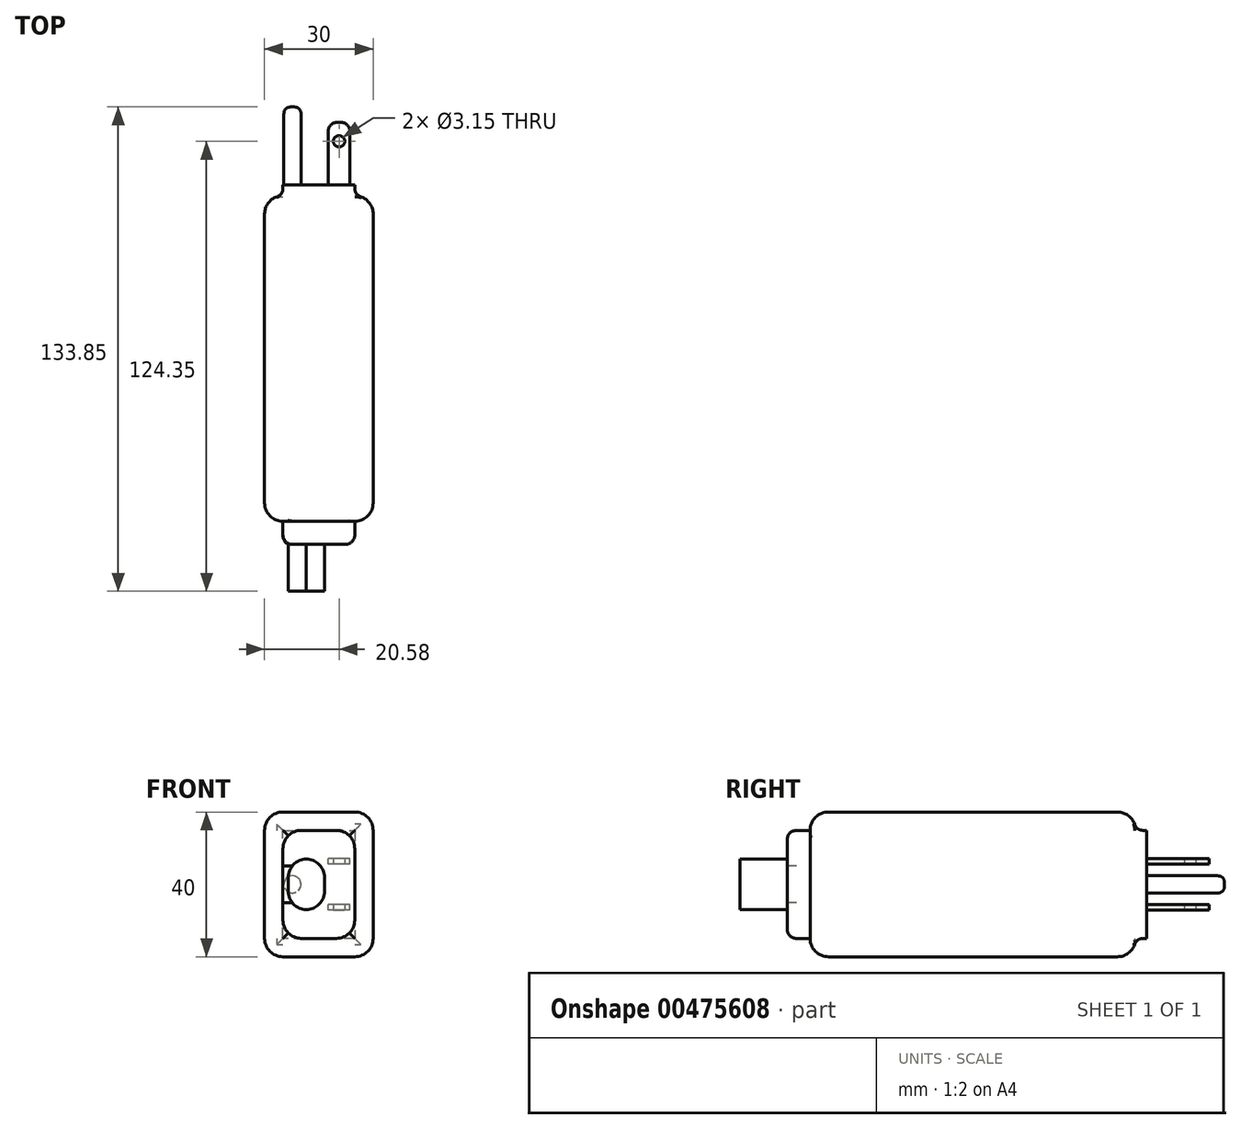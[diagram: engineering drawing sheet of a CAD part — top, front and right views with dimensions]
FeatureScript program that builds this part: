
annotation { "Feature Type Name" : "Feature", "Feature Type Description" : "" }
export const myFeature = defineFeature(function(context is Context, id is Id, definition is map)
    precondition{}
    {
        {
            var Q0;
            Q0=qCreatedBy(makeId("Top.planeOp"),FACE);
            var sketch = newSketch(context, id + "F0", { "sketchPlane" : qUnion([Q0])});
            skLineSegment(sketch, "E0.bottom", {"start": v(0, 0) * mm, "end": v(30, 0) * mm});
            skLineSegment(sketch, "E0.top", {"start": v(0, -90) * mm, "end": v(30, -90) * mm});
            skLineSegment(sketch, "E0.left", {"start": v(0, 0) * mm, "end": v(0, -90) * mm});
            skLineSegment(sketch, "E0.right", {"start": v(30, 0) * mm, "end": v(30, -90) * mm});
            skSolve(sketch);
        }
        {
            var Q0;
            Q0 = qSketchRegion(id + "F0", true);
            extrude(context, id + "F1", {"entities" : qUnion([Q0]), "depth" : 40 * mm});
        }
        {
            var Q0;
            Q0=makeQuery(id+"F1.opExtrude","CAP_EDGE",EDGE,{"disambiguationData":[OSD([sQuery(id+"F0.wireOp",EDGE,"E0.top")])],"isStart":false});
            var Q1;
            Q1=makeQuery(id+"F1.opExtrude","CAP_EDGE",EDGE,{"disambiguationData":[OSD([sQuery(id+"F0.wireOp",EDGE,"E0.bottom")])],"isStart":false});
            var Q2;
            Q2=makeQuery(id+"F1.opExtrude","CAP_EDGE",EDGE,{"disambiguationData":[OSD([sQuery(id+"F0.wireOp",EDGE,"E0.right")])],"isStart":false});
            var Q3;
            Q3=makeQuery(id+"F1.opExtrude","CAP_EDGE",EDGE,{"disambiguationData":[OSD([sQuery(id+"F0.wireOp",EDGE,"E0.left")])],"isStart":false});
            var Q4;
            Q4=makeQuery(id+"F1.opExtrude","CAP_EDGE",EDGE,{"disambiguationData":[OSD([sQuery(id+"F0.wireOp",EDGE,"E0.right")])],"isStart":true});
            var Q5;
            Q5=makeQuery(id+"F1.opExtrude","SWEPT_EDGE",EDGE,{"disambiguationData":[OSD([sQuery(id+"F0.wireOp",EDGE,"E0.top"),sQuery(id+"F0.wireOp",EDGE,"E0.right")])]});
            var Q6;
            Q6=makeQuery(id+"F1.opExtrude","SWEPT_EDGE",EDGE,{"disambiguationData":[OSD([sQuery(id+"F0.wireOp",EDGE,"E0.top"),sQuery(id+"F0.wireOp",EDGE,"E0.left")])]});
            var Q7;
            Q7=makeQuery(id+"F1.opExtrude","CAP_EDGE",EDGE,{"disambiguationData":[OSD([sQuery(id+"F0.wireOp",EDGE,"E0.top")])],"isStart":true});
            var Q8;
            Q8=makeQuery(id+"F1.opExtrude","SWEPT_EDGE",EDGE,{"disambiguationData":[OSD([sQuery(id+"F0.wireOp",EDGE,"E0.bottom"),sQuery(id+"F0.wireOp",EDGE,"E0.right")])]});
            var Q9;
            Q9=makeQuery(id+"F1.opExtrude","SWEPT_EDGE",EDGE,{"disambiguationData":[OSD([sQuery(id+"F0.wireOp",EDGE,"E0.bottom"),sQuery(id+"F0.wireOp",EDGE,"E0.left")])]});
            var Q10;
            Q10=makeQuery(id+"F1.opExtrude","CAP_EDGE",EDGE,{"disambiguationData":[OSD([sQuery(id+"F0.wireOp",EDGE,"E0.bottom")])],"isStart":true});
            var Q11;
            Q11=makeQuery(id+"F1.opExtrude","CAP_EDGE",EDGE,{"disambiguationData":[OSD([sQuery(id+"F0.wireOp",EDGE,"E0.left")])],"isStart":true});
            fillet(context, id + "F2", {"entities" : qUnion([Q0, Q1, Q2, Q3, Q4, Q5, Q6, Q7, Q8, Q9, Q10, Q11]), "radius" : 5.08 * mm, "tangentPropagation" : true, "allowEdgeOverflow" : false});
        }
        {
            var Q0;
            Q0=makeQuery(id+"F1.opExtrude","SWEPT_FACE",FACE,{"disambiguationData":[OSD([sQuery(id+"F0.wireOp",EDGE,"E0.bottom")])]});
            var sketch = newSketch(context, id + "F3", { "sketchPlane" : qUnion([Q0])});
            skLineSegment(sketch, "E1", {"start": v(-15, 34.92) * mm, "end": v(-15, 5.08) * mm, "construction": true});
            skLineSegment(sketch, "E2", {"start": v(-24.92, 20) * mm, "end": v(-5.08, 20) * mm, "construction": true});
            skLineSegment(sketch, "E3.bottom", {"start": v(-20, 23.5) * mm, "end": v(-10, 23.5) * mm});
            skLineSegment(sketch, "E3.top", {"start": v(-20, 16.5) * mm, "end": v(-10, 16.5) * mm});
            skLineSegment(sketch, "E3.left", {"start": v(-20, 23.5) * mm, "end": v(-20, 16.5) * mm});
            skLineSegment(sketch, "E3.right", {"start": v(-10, 23.5) * mm, "end": v(-10, 16.5) * mm});
            skSolve(sketch);
        }
        {
            var Q0;
            Q0=makeQuery(id+"F3.imprint","IMPRINT",FACE,{"disambiguationData":[TD([[makeQuery(id+"F3.imprint","IMPRINT",EDGE,{"derivedFrom":sQuery(id+"F3.wireOp",EDGE,"E3.bottom")}),1.0]])]});
            var Q1;
            Q1=makeQuery(id+"F3.imprint","IMPRINT",FACE,{"disambiguationData":[TD([[makeQuery(id+"F3.imprint","IMPRINT",EDGE,{"derivedFrom":sQuery(id+"F3.wireOp",EDGE,"E3.bottom")}),-1.0]])]});
            extrude(context, id + "F4", {"entities" : qUnion([Q0, Q1]), "operationType" : NewBodyOperationType.ADD, "depth" : 3 * mm});
        }
        {
            var Q0;
            {var subQ0=sQuery(id+"F0.wireOp",EDGE,"E0.left");var subQ1=sQuery(id+"F0.wireOp",EDGE,"E0.bottom");Q0=makeQuery(id+"F4.boolean.opBoolean","MERGE",EDGE,{"derivedFrom":[makeQuery(id+"F2.opFillet","BLEND_EDGE",EDGE,{"blendedFrom":[makeQuery(id+"F1.opExtrude","SWEPT_EDGE",EDGE,{"disambiguationData":[OSD([subQ1,subQ0])]}),makeQuery(id+"F1.opExtrude","SWEPT_FACE",FACE,{"disambiguationData":[OSD([subQ1])]})],"blendedInto":[makeQuery(id+"F1.opExtrude","SWEPT_FACE",FACE,{"disambiguationData":[OSD([subQ1])]})]}),makeQuery(id+"F4.opExtrude","CAP_EDGE",EDGE,{"disambiguationData":[OSD([subQ1,subQ0])],"isStart":true})]});}
            var Q1;
            {var subQ0=sQuery(id+"F0.wireOp",EDGE,"E0.bottom");var subQ1=makeQuery(id+"F2.opFillet","BLEND_EDGE",EDGE,{"blendedFrom":[makeQuery(id+"F1.opExtrude","CAP_EDGE",EDGE,{"disambiguationData":[OSD([subQ0])],"isStart":true}),makeQuery(id+"F1.opExtrude","SWEPT_FACE",FACE,{"disambiguationData":[OSD([subQ0])]})],"blendedInto":[makeQuery(id+"F1.opExtrude","SWEPT_FACE",FACE,{"disambiguationData":[OSD([subQ0])]})]});Q1=makeQuery(id+"F4.boolean.opBoolean","MERGE",EDGE,{"derivedFrom":[subQ1,makeQuery(id+"F4.opExtrude","CAP_EDGE",EDGE,{"disambiguationData":[OSD([subQ0]),TDD([makeQuery(id+"F3.imprint","IMPRINT",EDGE,{"derivedFrom":subQ1})])],"isStart":true})]});}
            var Q2;
            {var subQ0=sQuery(id+"F0.wireOp",EDGE,"E0.bottom");var subQ1=makeQuery(id+"F2.opFillet","BLEND_EDGE",EDGE,{"blendedFrom":[makeQuery(id+"F1.opExtrude","CAP_EDGE",EDGE,{"disambiguationData":[OSD([subQ0])],"isStart":false}),makeQuery(id+"F1.opExtrude","SWEPT_FACE",FACE,{"disambiguationData":[OSD([subQ0])]})],"blendedInto":[makeQuery(id+"F1.opExtrude","SWEPT_FACE",FACE,{"disambiguationData":[OSD([subQ0])]})]});Q2=makeQuery(id+"F4.boolean.opBoolean","MERGE",EDGE,{"derivedFrom":[subQ1,makeQuery(id+"F4.opExtrude","CAP_EDGE",EDGE,{"disambiguationData":[OSD([subQ0]),TDD([makeQuery(id+"F3.imprint","IMPRINT",EDGE,{"derivedFrom":subQ1})])],"isStart":true})]});}
            var Q3;
            {var subQ0=sQuery(id+"F0.wireOp",EDGE,"E0.right");var subQ1=sQuery(id+"F0.wireOp",EDGE,"E0.bottom");Q3=makeQuery(id+"F4.boolean.opBoolean","MERGE",EDGE,{"derivedFrom":[makeQuery(id+"F2.opFillet","BLEND_EDGE",EDGE,{"blendedFrom":[makeQuery(id+"F1.opExtrude","SWEPT_EDGE",EDGE,{"disambiguationData":[OSD([subQ1,subQ0])]}),makeQuery(id+"F1.opExtrude","SWEPT_FACE",FACE,{"disambiguationData":[OSD([subQ1])]})],"blendedInto":[makeQuery(id+"F1.opExtrude","SWEPT_FACE",FACE,{"disambiguationData":[OSD([subQ1])]})]}),makeQuery(id+"F4.opExtrude","CAP_EDGE",EDGE,{"disambiguationData":[OSD([subQ1,subQ0])],"isStart":true})]});}
            fillet(context, id + "F5", {"entities" : qUnion([Q0, Q1, Q2, Q3]), "radius" : 2.54 * mm, "tangentPropagation" : true, "rho" : 0.5, "crossSection" : FilletCrossSection.CONIC, "allowEdgeOverflow" : false});
        }
        {
            var Q0;
            Q0=makeQuery(id+"F4.opExtrude","CAP_FACE",FACE,{"disambiguationData":[OSD([sQuery(id+"F0.wireOp",EDGE,"E0.bottom"),sQuery(id+"F0.wireOp",EDGE,"E0.left"),sQuery(id+"F0.wireOp",EDGE,"E0.right")])],"isStart":false});
            var sketch = newSketch(context, id + "F6", { "sketchPlane" : qUnion([Q0])});
            skLineSegment(sketch, "E4", {"start": v(-24.92, 20) * mm, "end": v(-5.08, 20) * mm, "construction": true});
            skLineSegment(sketch, "E5", {"start": v(-15, 5.08) * mm, "end": v(-15, 34.92) * mm, "construction": true});
            skLineSegment(sketch, "E6.bottom", {"start": v(-23.58, 12.92) * mm, "end": v(-17.58, 12.92) * mm});
            skLineSegment(sketch, "E6.top", {"start": v(-23.58, 14.42) * mm, "end": v(-17.58, 14.42) * mm});
            skLineSegment(sketch, "E6.left", {"start": v(-23.58, 12.93) * mm, "end": v(-23.58, 14.42) * mm});
            skLineSegment(sketch, "E6.right", {"start": v(-17.58, 12.93) * mm, "end": v(-17.58, 14.43) * mm});
            skLineSegment(sketch, "E7.bottom", {"start": v(-23.58, 25.57) * mm, "end": v(-17.58, 25.57) * mm});
            skLineSegment(sketch, "E7.top", {"start": v(-23.58, 27.08) * mm, "end": v(-17.58, 27.08) * mm});
            skLineSegment(sketch, "E7.left", {"start": v(-23.58, 25.57) * mm, "end": v(-23.58, 27.08) * mm});
            skLineSegment(sketch, "E7.right", {"start": v(-17.58, 25.57) * mm, "end": v(-17.58, 27.08) * mm});
            skSolve(sketch);
        }
        {
            var Q0;
            Q0 = qSketchRegion(id + "F6", true);
            extrude(context, id + "F7", {"entities" : qUnion([Q0]), "operationType" : NewBodyOperationType.ADD, "depth" : 17.25 * mm});
        }
        {
            var Q0;
            Q0=makeQuery(id+"F7.opExtrude","CAP_EDGE",EDGE,{"disambiguationData":[OSD([sQuery(id+"F6.wireOp",EDGE,"E6.left")])],"isStart":false});
            var Q1;
            Q1=makeQuery(id+"F7.opExtrude","CAP_EDGE",EDGE,{"disambiguationData":[OSD([sQuery(id+"F6.wireOp",EDGE,"E7.left")])],"isStart":false});
            var Q2;
            Q2=makeQuery(id+"F7.opExtrude","CAP_EDGE",EDGE,{"disambiguationData":[OSD([sQuery(id+"F6.wireOp",EDGE,"E6.right")])],"isStart":false});
            var Q3;
            Q3=makeQuery(id+"F7.opExtrude","CAP_EDGE",EDGE,{"disambiguationData":[OSD([sQuery(id+"F6.wireOp",EDGE,"E7.right")])],"isStart":false});
            fillet(context, id + "F8", {"entities" : qUnion([Q0, Q1, Q2, Q3]), "radius" : 2.54 * mm, "tangentPropagation" : true, "allowEdgeOverflow" : false});
        }
        {
            var Q0;
            Q0=makeQuery(id+"F4.opExtrude","CAP_FACE",FACE,{"disambiguationData":[OSD([sQuery(id+"F0.wireOp",EDGE,"E0.bottom"),sQuery(id+"F0.wireOp",EDGE,"E0.left"),sQuery(id+"F0.wireOp",EDGE,"E0.right")])],"isStart":false});
            var sketch = newSketch(context, id + "F9", { "sketchPlane" : qUnion([Q0])});
            skCircle(sketch, "E8", {"center": v(-7.7, 20) * mm, "radius": 2.38 * mm});
            skLineSegment(sketch, "E9", {"start": v(-24.92, 20) * mm, "end": v(-5.08, 20) * mm, "construction": true});
            skSolve(sketch);
        }
        {
            var Q0;
            Q0 = qSketchRegion(id + "F9", true);
            extrude(context, id + "F10", {"entities" : qUnion([Q0]), "operationType" : NewBodyOperationType.ADD, "depth" : 21.5 * mm});
        }
        {
            var Q0;
            Q0=makeQuery(id+"F10.opExtrude","CAP_FACE",FACE,{"disambiguationData":[OSD([sQuery(id+"F9.wireOp",EDGE,"E8")])],"isStart":false});
            fillet(context, id + "F11", {"entities" : qUnion([Q0]), "radius" : 2 * mm, "tangentPropagation" : true, "rho" : 0.5, "crossSection" : FilletCrossSection.CONIC, "allowEdgeOverflow" : false});
        }
        {
            var Q0;
            Q0=makeQuery(id+"F7.opExtrude","SWEPT_FACE",FACE,{"disambiguationData":[OSD([sQuery(id+"F6.wireOp",EDGE,"E6.bottom")])]});
            var sketch = newSketch(context, id + "F12", { "sketchPlane" : qUnion([Q0])});
            skLineSegment(sketch, "E10", {"start": v(23.58, -15) * mm, "end": v(17.58, -15) * mm, "construction": true});
            skCircle(sketch, "E11", {"center": v(20.58, -15) * mm, "radius": 1.57 * mm});
            skSolve(sketch);
        }
        {
            var Q0;
            Q0 = qSketchRegion(id + "F12", true);
            extrude(context, id + "F13", {"entities" : qUnion([Q0]), "operationType" : NewBodyOperationType.REMOVE, "oppositeDirection" : true, "depth" : 25.4 * mm});
        }
        {
            var Q0;
            Q0=makeQuery(id+"F1.opExtrude","SWEPT_FACE",FACE,{"disambiguationData":[OSD([sQuery(id+"F0.wireOp",EDGE,"E0.top")])]});
            var sketch = newSketch(context, id + "F14", { "sketchPlane" : qUnion([Q0])});
            skLineSegment(sketch, "E12.0.0", {"start": v(5.08, 34.92) * mm, "end": v(5.08, 5.08) * mm});
            skLineSegment(sketch, "E12.0.1", {"start": v(5.08, 5.08) * mm, "end": v(24.92, 5.08) * mm});
            skLineSegment(sketch, "E12.0.2", {"start": v(24.92, 5.08) * mm, "end": v(24.92, 34.92) * mm});
            skLineSegment(sketch, "E12.0.3", {"start": v(24.92, 34.92) * mm, "end": v(5.08, 34.92) * mm});
            skSolve(sketch);
        }
        {
            var Q0;
            Q0 = qSketchRegion(id + "F14", true);
            extrude(context, id + "F15", {"entities" : qUnion([Q0]), "operationType" : NewBodyOperationType.ADD, "depth" : 6.35 * mm});
        }
        {
            var Q0;
            Q0=makeQuery(id+"F15.opExtrude","SWEPT_EDGE",EDGE,{"disambiguationData":[OSD([sQuery(id+"F14.wireOp",EDGE,"E12.0.1"),sQuery(id+"F14.wireOp",EDGE,"E12.0.2")])]});
            var Q1;
            Q1=makeQuery(id+"F15.opExtrude","SWEPT_EDGE",EDGE,{"disambiguationData":[OSD([sQuery(id+"F14.wireOp",EDGE,"E12.0.0"),sQuery(id+"F14.wireOp",EDGE,"E12.0.1")])]});
            var Q2;
            Q2=makeQuery(id+"F15.opExtrude","SWEPT_EDGE",EDGE,{"disambiguationData":[OSD([sQuery(id+"F14.wireOp",EDGE,"E12.0.2"),sQuery(id+"F14.wireOp",EDGE,"E12.0.3")])]});
            var Q3;
            Q3=makeQuery(id+"F15.opExtrude","SWEPT_EDGE",EDGE,{"disambiguationData":[OSD([sQuery(id+"F14.wireOp",EDGE,"E12.0.0"),sQuery(id+"F14.wireOp",EDGE,"E12.0.3")])]});
            fillet(context, id + "F16", {"entities" : qUnion([Q0, Q1, Q2, Q3]), "radius" : 5.08 * mm, "tangentPropagation" : true, "allowEdgeOverflow" : false});
        }
        {
            var Q0;
            Q0=makeQuery(id+"F15.opExtrude","CAP_FACE",FACE,{"disambiguationData":[OSD([sQuery(id+"F14.wireOp",EDGE,"E12.0.0"),sQuery(id+"F14.wireOp",EDGE,"E12.0.1"),sQuery(id+"F14.wireOp",EDGE,"E12.0.2"),sQuery(id+"F14.wireOp",EDGE,"E12.0.3")])],"isStart":false});
            var sketch = newSketch(context, id + "F17", { "sketchPlane" : qUnion([Q0])});
            skLineSegment(sketch, "E13.bottom", {"start": v(6.54, 27) * mm, "end": v(16.54, 27) * mm});
            skLineSegment(sketch, "E13.top", {"start": v(6.54, 13) * mm, "end": v(16.54, 13) * mm});
            skLineSegment(sketch, "E13.left", {"start": v(6.54, 27) * mm, "end": v(6.54, 13) * mm});
            skLineSegment(sketch, "E13.right", {"start": v(16.54, 27) * mm, "end": v(16.54, 13) * mm});
            skPoint(sketch, "E13.middle", {"position": v(11.54, 20) * mm});
            skPoint(sketch, "E13.middle.positionSnap0", {"position": v(5.08, 20) * mm});
            skPoint(sketch, "E13.centerSnap0", {"position": v(5.08, 20) * mm});
            skSolve(sketch);
        }
        {
            var Q0;
            Q0 = qSketchRegion(id + "F17", true);
            extrude(context, id + "F18", {"entities" : qUnion([Q0]), "operationType" : NewBodyOperationType.ADD, "depth" : 13 * mm});
        }
        {
            var Q0;
            Q0=makeQuery(id+"F18.opExtrude","SWEPT_EDGE",EDGE,{"disambiguationData":[OSD([sQuery(id+"F17.wireOp",EDGE,"E13.top"),sQuery(id+"F17.wireOp",EDGE,"E13.right")])]});
            var Q1;
            Q1=makeQuery(id+"F18.opExtrude","SWEPT_EDGE",EDGE,{"disambiguationData":[OSD([sQuery(id+"F17.wireOp",EDGE,"E13.top"),sQuery(id+"F17.wireOp",EDGE,"E13.left")])]});
            var Q2;
            Q2=makeQuery(id+"F18.opExtrude","SWEPT_EDGE",EDGE,{"disambiguationData":[OSD([sQuery(id+"F17.wireOp",EDGE,"E13.bottom"),sQuery(id+"F17.wireOp",EDGE,"E13.right")])]});
            var Q3;
            Q3=makeQuery(id+"F18.opExtrude","SWEPT_EDGE",EDGE,{"disambiguationData":[OSD([sQuery(id+"F17.wireOp",EDGE,"E13.bottom"),sQuery(id+"F17.wireOp",EDGE,"E13.left")])]});
            fillet(context, id + "F19", {"entities" : qUnion([Q0, Q1, Q2, Q3]), "radius" : 5.08 * mm, "tangentPropagation" : true, "allowEdgeOverflow" : false});
        }
        {
            var Q0;
            Q0=makeQuery(id+"F15.opExtrude","CAP_EDGE",EDGE,{"disambiguationData":[OSD([sQuery(id+"F14.wireOp",EDGE,"E12.0.2")])],"isStart":false});
            fillet(context, id + "F20", {"entities" : qUnion([Q0]), "radius" : 2.54 * mm, "tangentPropagation" : true, "allowEdgeOverflow" : false});
        }
    });
